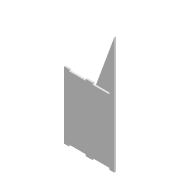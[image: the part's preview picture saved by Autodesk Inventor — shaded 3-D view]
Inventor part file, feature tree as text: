
AUTODESK INVENTOR PART (.ipt)
format: ipt  version: 2022 (Build 260153000, 153)  size: 120,832 bytes
history: native  units: mm
features: extrude x2, sketch x2, other x2, reference x1
ambient origin geometry x8: Origin, YZ Plane, XZ Plane, XY Plane, X Axis, Y Axis, Z Axis, Center Point
bodies: Solid1 (feature_tree)
feature tree (7):
  extrude  "Extrusion1"  Depth=5.0mm
  extrude  "Extrusion2"  Depth=5.0mm
  sketch  "Sketch1"  dims[d0=50.0mm d1=5.0mm]
  reference  "Reference1"
  sketch  "Sketch2"  dims[d2=50.0mm d3=5.0mm d4=20.0mm d5=15.0mm d6=50.0mm d7=5.0mm d8=5.0mm d9=15.0mm d10=5.0mm d11=0.0mm d12=5.0mm d13=50.0mm d14=5.0mm d15=50.0mm d16=30.0mm d17=30.0mm d18=5.0mm d19=0.0mm]
  other  "Assembly2"
  other  "Modelo base:1"
